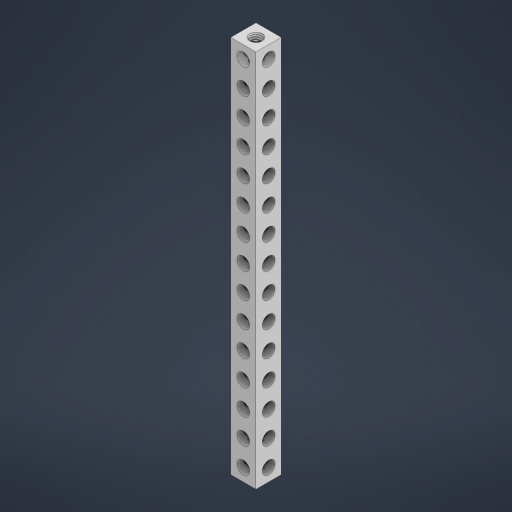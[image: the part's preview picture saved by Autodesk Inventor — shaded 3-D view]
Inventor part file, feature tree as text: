
AUTODESK INVENTOR PART (.ipt)
format: ipt  version: 2023 (Build 270158000, 158)  size: 1,337,344 bytes
history: native  units: in
note: dims shown in document units (in); Inventor stores cm internally (conversion verified against a paired STEP export)
features: mirror x1
ambient origin geometry x8: Origin, YZ Plane, XZ Plane, XY Plane, X Axis, Y Axis, Z Axis, Center Point
bodies: Solid1 (feature_tree)
feature tree (1):
  mirror  "Mirror3"
